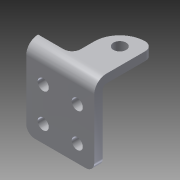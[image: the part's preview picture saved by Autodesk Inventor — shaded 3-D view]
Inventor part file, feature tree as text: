
AUTODESK INVENTOR PART (.ipt)
format: ipt  version: 2014 (Build 180170000, 170)  size: 218,112 bytes
history: native  units: in
note: dims shown in document units (in); Inventor stores cm internally (conversion verified against a paired STEP export)
features: sheet_metal_op x4, sketch x3, other x3, extrude x1, fillet x1
ambient origin geometry x8: Origin, YZ Plane, XZ Plane, XY Plane, X Axis, Y Axis, Z Axis, Center Point
bodies: Solid1 (feature_tree)
feature tree (12):
  sheet_metal_op  "Face1"
  sheet_metal_op  "Flange1"
  extrude  "Extrusion1"  Depth=1.0in
  fillet  "Fillet1"  Radius=0.163in
  sketch  "Sketch1"  dims[d0=1.0in d1=1.0in d2=0.163in]
  other  "Plate1"
  sketch  "Sketch2"  dims[d3=0.25in]
  other  "Plate2"
  sheet_metal_op  "Bend1"
  sheet_metal_op  "Corner1"
  sketch  "Sketch3"  dims[d4=0.25in d5=0.7874in d7=0.5in d8=0.7874in d10=0.5in d13=0.125in d14=0.125in d15=0.0625in d16=0.25in d17=0.125in d18=0.875in d19=90.0deg d20=0.05in d21=0.5in d22=0.125in d23=0.125in d24=0.187in d25=0.25in d26=0.25in d27=0.375in d28=0.125in d29=1.0in d30=0.0in d31=0.125in]
  other  "Definition1"
